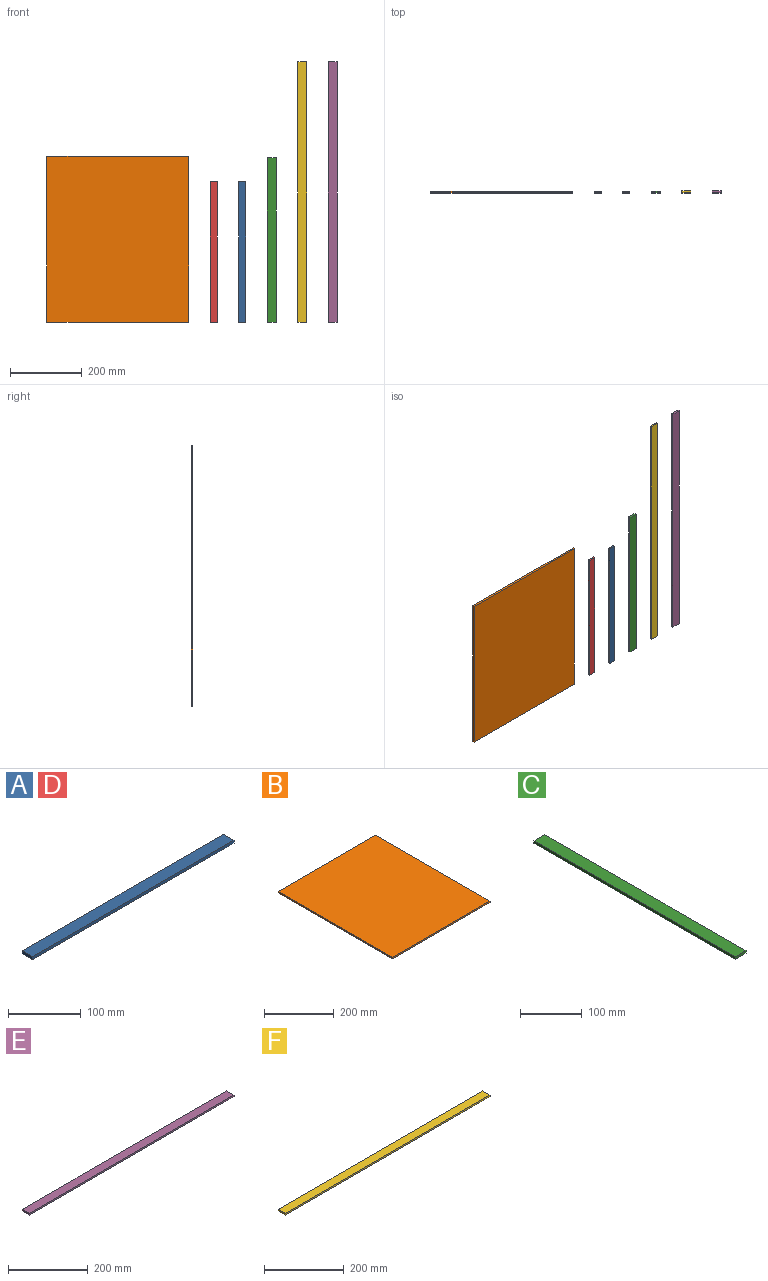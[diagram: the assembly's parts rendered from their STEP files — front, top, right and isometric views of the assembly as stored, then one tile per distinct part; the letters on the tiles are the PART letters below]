
ASSEMBLY  parts=6 mates=5
PART A: 6 faces, bbox 393x20x5 mm
  f0: plane 393x5mm, normal (0,1,0), area 1965mm2, adj f1,f3,f4,f5
  f1: plane 20x5mm, normal (-1,0,0), area 100mm2, adj f0,f2,f4,f5
  f2: plane 393x5mm, normal (0,-1,0), area 1965mm2, adj f1,f3,f4,f5
  f3: plane 20x5mm, normal (1,0,0), area 100mm2, adj f0,f2,f4,f5
  f4: plane 393x20mm, normal (0,0,1), area 7860mm2, adj f0,f1,f2,f3
  f5: plane 393x20mm, normal (0,0,-1), area 7860mm2, adj f0,f1,f2,f3
PART B: 6 faces, bbox 397x464x5 mm
  f0: plane 397x5mm, normal (0,1,0), area 1985mm2, adj f1,f3,f4,f5
  f1: plane 464x5mm, normal (-1,0,0), area 2320mm2, adj f0,f2,f4,f5
  f2: plane 397x5mm, normal (0,-1,0), area 1985mm2, adj f1,f3,f4,f5
  f3: plane 464x5mm, normal (1,0,0), area 2320mm2, adj f0,f2,f4,f5
  f4: plane 464x397mm, normal (0,0,-1), area 184208mm2, adj f0,f1,f2,f3
  f5: plane 464x397mm, normal (0,0,1), area 184208mm2, adj f0,f1,f2,f3
PART C: 6 faces, bbox 25x460x5 mm
  f0: plane 25x5mm, normal (0,1,0), area 125mm2, adj f1,f3,f4,f5
  f1: plane 460x5mm, normal (-1,0,0), area 2300mm2, adj f0,f2,f4,f5
  f2: plane 25x5mm, normal (0,-1,0), area 125mm2, adj f1,f3,f4,f5
  f3: plane 460x5mm, normal (1,0,0), area 2300mm2, adj f0,f2,f4,f5
  f4: plane 460x25mm, normal (0,0,1), area 11500mm2, adj f0,f1,f2,f3
  f5: plane 460x25mm, normal (0,0,-1), area 11500mm2, adj f0,f1,f2,f3
PART D: same geometry as A
PART E: 6 faces, bbox 729x25x5 mm
  f0: plane 729x5mm, normal (0,1,0), area 3645mm2, adj f1,f3,f4,f5
  f1: plane 25x5mm, normal (-1,0,0), area 125mm2, adj f0,f2,f4,f5
  f2: plane 729x5mm, normal (0,-1,0), area 3645mm2, adj f1,f3,f4,f5
  f3: plane 25x5mm, normal (1,0,0), area 125mm2, adj f0,f2,f4,f5
  f4: plane 729x25mm, normal (0,0,1), area 18225mm2, adj f0,f1,f2,f3
  f5: plane 729x25mm, normal (0,0,-1), area 18225mm2, adj f0,f1,f2,f3
PART F: 6 faces, bbox 729x25x5 mm
  f0: plane 729x5mm, normal (0,1,0), area 3645mm2, adj f1,f3,f4,f5
  f1: plane 25x5mm, normal (-1,0,0), area 125mm2, adj f0,f2,f4,f5
  f2: plane 729x5mm, normal (0,-1,0), area 3645mm2, adj f1,f3,f4,f5
  f3: plane 25x5mm, normal (1,0,0), area 125mm2, adj f0,f2,f4,f5
  f4: plane 729x25mm, normal (0,0,1), area 18225mm2, adj f0,f1,f2,f3
  f5: plane 729x25mm, normal (0,0,-1), area 18225mm2, adj f0,f1,f2,f3
PLACE A rot(axis=(-0.58,-0.58,-0.58),120deg) t=(-2055,0,32)mm
PLACE B rot(axis=(-1,0,0),90deg) t=(-830,5,0)mm
PLACE C rot(axis=(1,0,0),90deg) t=(-175,5,480)mm
PLACE D rot(axis=(-0.58,-0.58,-0.58),120deg) t=(-2135,0,32)mm
PLACE E rot(axis=(0.58,0.58,-0.58),120deg) t=(-5,5,5)mm
PLACE F rot(axis=(0.58,-0.58,0.58),120deg) t=(-590,5,724)mm
MATE fastened F.f4 <-> C.f4  axis (0,-1,0) through (-110,0,0)mm
MATE fastened C.f4 <-> A.f5  axis (0,-1,0) through (-195,0,0)mm
MATE fastened E.f4 <-> F.f4  axis (0,-1,0) through (-25,0,0)mm
MATE fastened D.f5 <-> B.f4  axis (0,-1,0) through (-355,0,0)mm
MATE fastened A.f5 <-> D.f5  axis (0,-1,0) through (-275,0,0)mm
